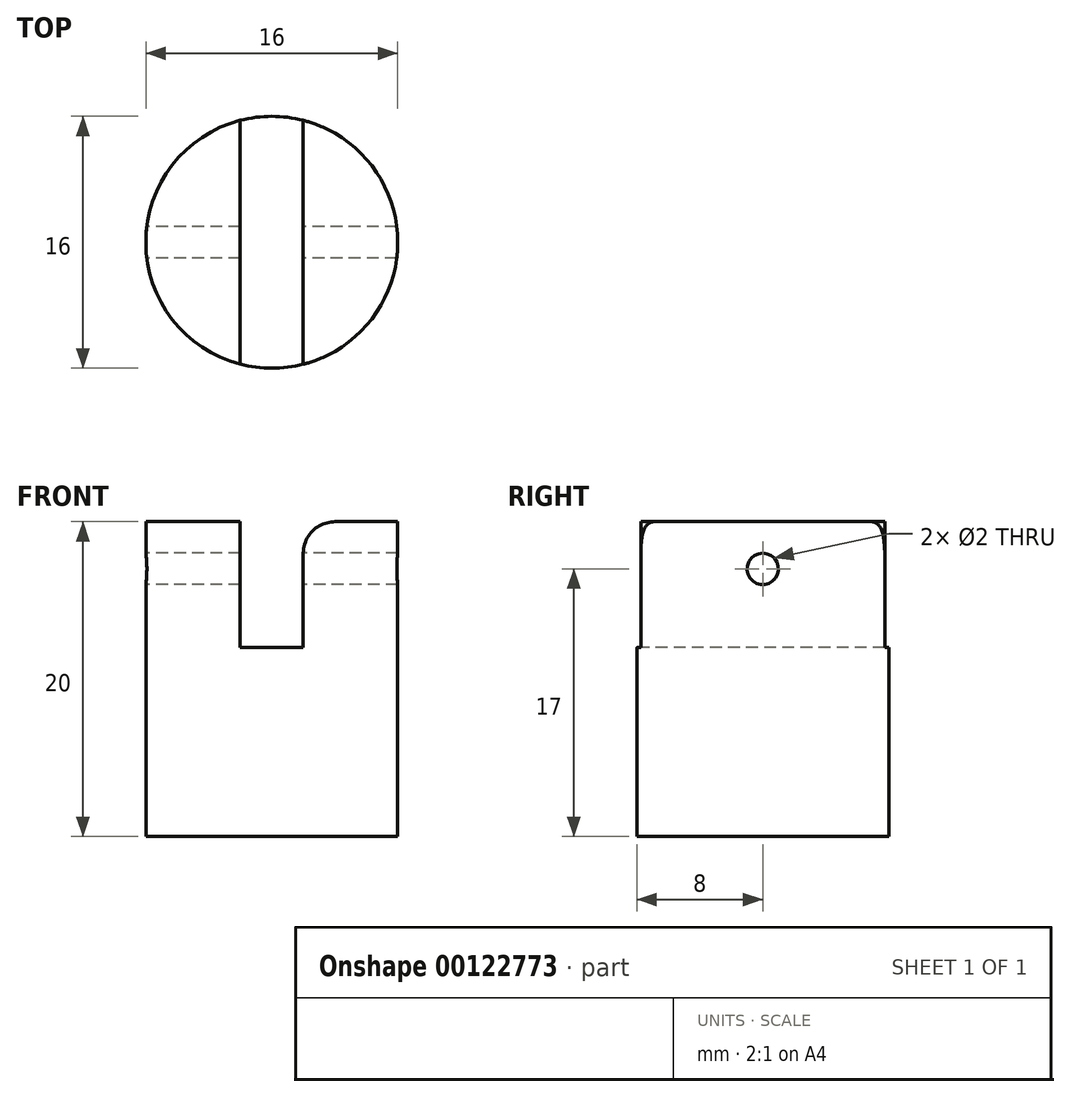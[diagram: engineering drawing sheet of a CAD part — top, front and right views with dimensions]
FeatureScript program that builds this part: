
annotation { "Feature Type Name" : "Feature", "Feature Type Description" : "" }
export const myFeature = defineFeature(function(context is Context, id is Id, definition is map)
    precondition{}
    {
        {
            var Q0;
            Q0=qCreatedBy(makeId("Top.planeOp"),FACE);
            var sketch = newSketch(context, id + "F0", { "sketchPlane" : qUnion([Q0])});
            skCircle(sketch, "E0", {"center": v(0, 0) * mm, "radius": 8 * mm});
            skSolve(sketch);
        }
        {
            var Q0;
            Q0=qSketchRegion(id+"F0",true);
            extrude(context, id + "F1", {"entities" : qUnion([Q0]), "endBound" : BoundingType.SYMMETRIC, "depth" : 20 * mm});
        }
        {
            var Q0;
            Q0=makeQuery(id+"F1.opExtrude","CAP_FACE",FACE,{"disambiguationData":[OSD([sQuery(id+"F0.wireOp",EDGE,"E0")])],"isStart":false});
            var sketch = newSketch(context, id + "F2", { "sketchPlane" : qUnion([Q0])});
            skLineSegment(sketch, "E1.bottom", {"start": v(-2, 10) * mm, "end": v(2, 10) * mm});
            skLineSegment(sketch, "E1.top", {"start": v(-2, -10) * mm, "end": v(2, -10) * mm});
            skLineSegment(sketch, "E1.left", {"start": v(-2, 10) * mm, "end": v(-2, -10) * mm});
            skLineSegment(sketch, "E1.right", {"start": v(2, 10) * mm, "end": v(2, -10) * mm});
            skPoint(sketch, "E1.middle", {"position": v(0, 0) * mm});
            skSolve(sketch);
        }
        {
            var Q0;
            Q0=qSketchRegion(id+"F2",true);
            extrude(context, id + "F3", {"entities" : qUnion([Q0]), "operationType" : NewBodyOperationType.REMOVE, "oppositeDirection" : true, "depth" : 8 * mm});
        }
        {
            var Q0;
            Q0=qCreatedBy(makeId("Right.planeOp"),FACE);
            var sketch = newSketch(context, id + "F4", { "sketchPlane" : qUnion([Q0])});
            skCircle(sketch, "E2", {"center": v(0, 7) * mm, "radius": 1 * mm});
            skSolve(sketch);
        }
        {
            var Q0;
            Q0=qSketchRegion(id+"F4",true);
            extrude(context, id + "F5", {"entities" : qUnion([Q0]), "operationType" : NewBodyOperationType.REMOVE, "endBound" : BoundingType.SYMMETRIC, "depth" : 25 * mm});
        }
        {
            var Q0;
            Q0=makeQuery(id+"F3.boolean.opBoolean","COPY",EDGE,{"derivedFrom":makeQuery(id+"F3.opExtrude","CAP_EDGE",EDGE,{"disambiguationData":[OSD([sQuery(id+"F2.wireOp",EDGE,"E1.left")])],"isStart":true})});
            var Q1;
            Q1=makeQuery(id+"F3.boolean.opBoolean","COPY",EDGE,{"derivedFrom":makeQuery(id+"F3.opExtrude","CAP_EDGE",EDGE,{"disambiguationData":[OSD([sQuery(id+"F2.wireOp",EDGE,"E1.right")])],"isStart":true})});
            fillet(context, id + "F6", {"entities" : qUnion([Q0, Q1]), "radius" : 2 * mm, "tangentPropagation" : true, "allowEdgeOverflow" : false});
        }
    });
